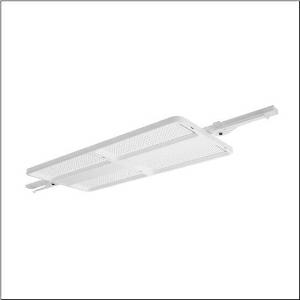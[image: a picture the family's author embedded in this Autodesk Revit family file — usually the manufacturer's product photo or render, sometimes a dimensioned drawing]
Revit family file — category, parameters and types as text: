
# Revit family: highbay_11_fur_modario_r__tragschiene_maxi_51hn11db4qma_85fe
name_source: partatom
category: Lighting Fixtures
units: mm (PartAtom-declared; Revit-internal decimal feet)

## family parameters
Cut with Voids When Loaded = No
Host = Face
Light Source = No
Part Type = Normal
Room Calculation Point = No
Round Connector Dimension = Use Diameter
Shared = No

## types (1)
- --- (1 x LED, 36000 lm, 177.7 W, 4000K)
    Apparent Load = 178 VA
    CIE Flux Codes = 85 97 100 100 100
    Color Rendering = 80
    Color Temperature = 4000K
    Default Elevation = 1800 mm
    Description = high bay luminaire Highbay 11 for Modario® trunking rail maxi; direct symmetric narrow distribution, light control with lens of PMMA; UGR ≤ 22 (X = 4H | Y = 8H | S = 0.25H | reflection values 70/50/20); luminous flux: 36.000lm; light colour: 840, colour temperature: 4000K, MacAdam ≤ 2 SDCM (initial), colour rendering: CRI > 80; luminous efficacy: 202,6lm/W; rated service life: 100.000h (L95/B50) at AT= 25°C; control: DALI 2; luminaire connection: plug, 5-pole, with phase selectionmains connection: 230..240V, AC 50/60Hz; connected load: 177,7W; protection rating (complete): IP64; insulation class (complete): insulation class I (protective earthing); protection symbol: D; impact resistance: IK07; certification: CE, ENEC, VDE, UKCA; internal wiring halogen-free; luminaire corresponds to IFS (International Featured Standards) requirements for safety and quality in the food industry; LABS conformity tested according to VDMA 24364:2018-05; housing frame of high-performance plastic PA6, matt traffic white (RAL 9016); cover of PMMA; fixing on rail side of steel, galvanised, white; blank cover of PC, traffic white (RAL 9016); dimension (LxWxH): 1.496 x 442 x 72mm; permissible operating ambient temperature: -40..+55°C (reducing of maximum allowable ambient temperature of 5°C with ceiling mounting); packaging unit: 1 piece
    Height = 72 mm  [stored 0.23622 ft]
    Lamp = 1 x LED
    Lamp Light Flux = 36000 lm
    Lamp Power = 177.7 W
    Lamp count = 1
    Length = 946 mm
    Luminous efficacy = 203 lm/W
    Manufacturer = Siteco
    ModVariant = No
    Model = 51HN11DB4QMA
    Mounting Place = Ceiling
    Mounting Type = Pendant
    Number of Poles = 1
    OnlyDefault = Yes
    Power Factor = 1
    Product Name = Highbay 11 für Modario® Tragschiene maxi
    Product group = high bay luminaire
    ProductGroupID = 901
    Protection Class = Protection class I
    Protection Degree = IP 64
    RLX_Detail_Level = 1
    RLX_Emergency_Light_Flux = 0 lm
    RLX_Emergency_Type = 0
    RLX_Emergency_Type_DB = No
    RlxData = <blob elided: 21453 chars, md5=d71da8fa>
    Socket = socket
    Standby Power = 0 W
    System Light Flux = 36000 lm
    System Power = 178 W
    Type Comments = factory setting: luminous flux: 100 % | dim-lin: 254 | 824 mA
    Type Image = l_1363248.jpg
    URL = http://relux.com
    VarID = @adj_023091
    Voltage = 0 V
    Weight = 0.00 kg
    Width = 442 mm

note: [stored X ft] marks values corroborated as IEEE doubles in the binary element streams (Revit-internal decimal feet)

## geometry (parser evidence)
native form markers: Blend x4, Sweep x10
no freeform markers — native parametric forms only
